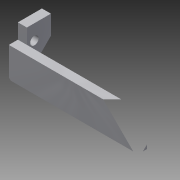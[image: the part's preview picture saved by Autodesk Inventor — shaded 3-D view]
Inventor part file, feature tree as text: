
AUTODESK INVENTOR PART (.ipt)
format: ipt  version: 2015 SP1 (Build 190203100, 203)  size: 164,352 bytes
history: native  units: mm
features: reference x6, sketch x5, fillet x4, extrude x3, hole x2
ambient origin geometry x8: Origin, YZ Plane, XZ Plane, XY Plane, X Axis, Y Axis, Z Axis, Center Point
bodies: Solid1 (feature_tree)
feature tree (20):
  extrude  "Extrusion1"  Depth=3.0mm
  extrude  "Extrusion2"  Depth=3.0mm
  hole  "Hole1"  [1 undecoded]
  extrude  "Extrusion3"  Depth=2.0mm
  hole  "Hole2"  [1 undecoded]
  fillet  "Fillet1"  Radius=3.0mm
  fillet  "Fillet4"  Radius=4.0mm
  fillet  "Fillet5"  Radius=4.0mm
  fillet  "Fillet6"  Radius=2.0mm
  sketch  "Sketch1"  dims[d0=43.0mm d1=3.0mm]
  sketch  "Sketch2"  dims[d2=10.0mm d3=0.0mm d4=3.0mm]
  sketch  "Sketch3"  dims[d5=20.0mm d6=8.0mm d7=0.0mm]
  reference  "Reference1"
  reference  "Reference2"
  sketch  "Sketch4"  dims[d8=2.8mm d9=6.0mm d10=4.0mm d11=2.0mm d12=90.0deg d13=8.0mm d14=20.594885mm d15=5.5mm]
  reference  "Reference3"
  reference  "Reference4"
  sketch  "Sketch5"  dims[d16=5.5mm d17=2.0mm d18=0.0mm d19=3.2mm d20=6.0mm d21=4.0mm d22=2.0mm d23=90.0deg d24=8.0mm d25=20.594885mm d26=3.0mm d29=4.0mm d30=4.0mm d31=2.0mm]
  reference  "Reference5"
  reference  "Reference6"
note: 2 required parameter values undecoded (feature->parameter linkage not recoverable at this tier; creation-order binding heuristic only, values carry confidence <= 0.55)
